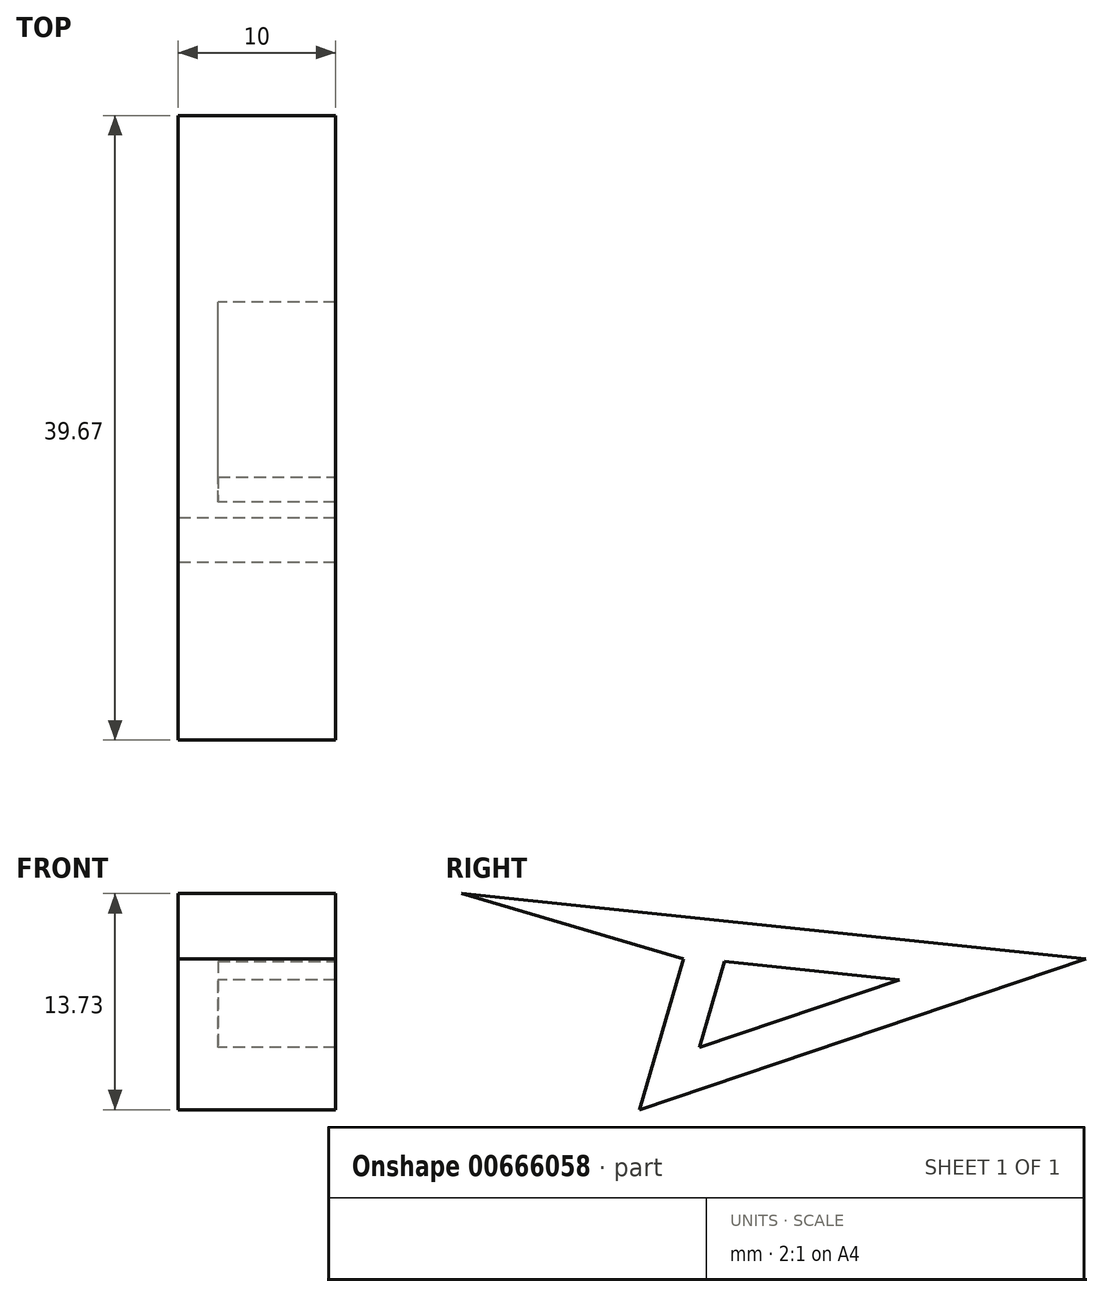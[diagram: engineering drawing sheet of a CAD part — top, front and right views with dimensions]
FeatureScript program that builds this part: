
annotation { "Feature Type Name" : "Feature", "Feature Type Description" : "" }
export const myFeature = defineFeature(function(context is Context, id is Id, definition is map)
    precondition{}
    {
        {
            var Q0;
            Q0=qCreatedBy(makeId("Right.planeOp"),FACE);
            var sketch = newSketch(context, id + "F0", { "sketchPlane" : qUnion([Q0])});
            skPoint(sketch, "E0.0", {"position": v(0, 0) * mm});
            skLineSegment(sketch, "E1", {"start": v(-14.1, 4.16) * mm, "end": v(25.56, 0) * mm});
            skLineSegment(sketch, "E2", {"start": v(-14.1, 4.16) * mm, "end": v(0, 0) * mm});
            skLineSegment(sketch, "E3", {"start": v(0, 0) * mm, "end": v(-2.82, -9.57) * mm});
            skLineSegment(sketch, "E4", {"start": v(-2.82, -9.57) * mm, "end": v(25.56, 0) * mm});
            skSolve(sketch);
        }
        {
            var Q0;
            Q0 = qSketchRegion(id + "F0", true);
            extrude(context, id + "F1", {"entities" : qUnion([Q0]), "depth" : 10 * mm, "offsetDistance" : 25.4 * mm});
        }
        {
            var Q0;
            Q0=makeQuery(id+"F1.opExtrude","CAP_FACE",FACE,{"disambiguationData":[OSD([sQuery(id+"F0.wireOp",EDGE,"E1"),sQuery(id+"F0.wireOp",EDGE,"E2"),sQuery(id+"F0.wireOp",EDGE,"E3"),sQuery(id+"F0.wireOp",EDGE,"E4")])],"isStart":false});
            shell(context, id + "F2", {"entities" : qUnion([Q0]), "thickness" : 2.54 * mm});
        }
    });
